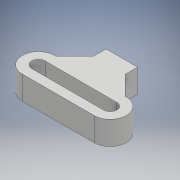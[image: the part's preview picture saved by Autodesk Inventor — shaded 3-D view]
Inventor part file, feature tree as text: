
AUTODESK INVENTOR PART (.ipt)
format: ipt  version: 2017 (Build 210142000, 142)  size: 125,440 bytes
history: native  units: mm
features: extrude x2, sketch x2, chamfer x1
ambient origin geometry x8: Origin, YZ Plane, XZ Plane, XY Plane, X Axis, Y Axis, Z Axis, Center Point
bodies: Solid1 (feature_tree)
feature tree (5):
  extrude  "Extrusion1"  Depth=6.0mm
  extrude  "Extrusion2"  Depth=20.0mm
  chamfer  "Chamfer1"  Distance=20.0mm
  sketch  "Sketch1"  dims[d0=8.5mm d1=6.0mm]
  sketch  "Sketch2"  dims[d2=45.72mm d3=20.0mm d4=20.0mm d5=15.0mm d6=0.0mm d7=7.0mm d8=15.0mm d9=0.0mm d10=12.25mm d11=2.0mm d12=45.0deg]
